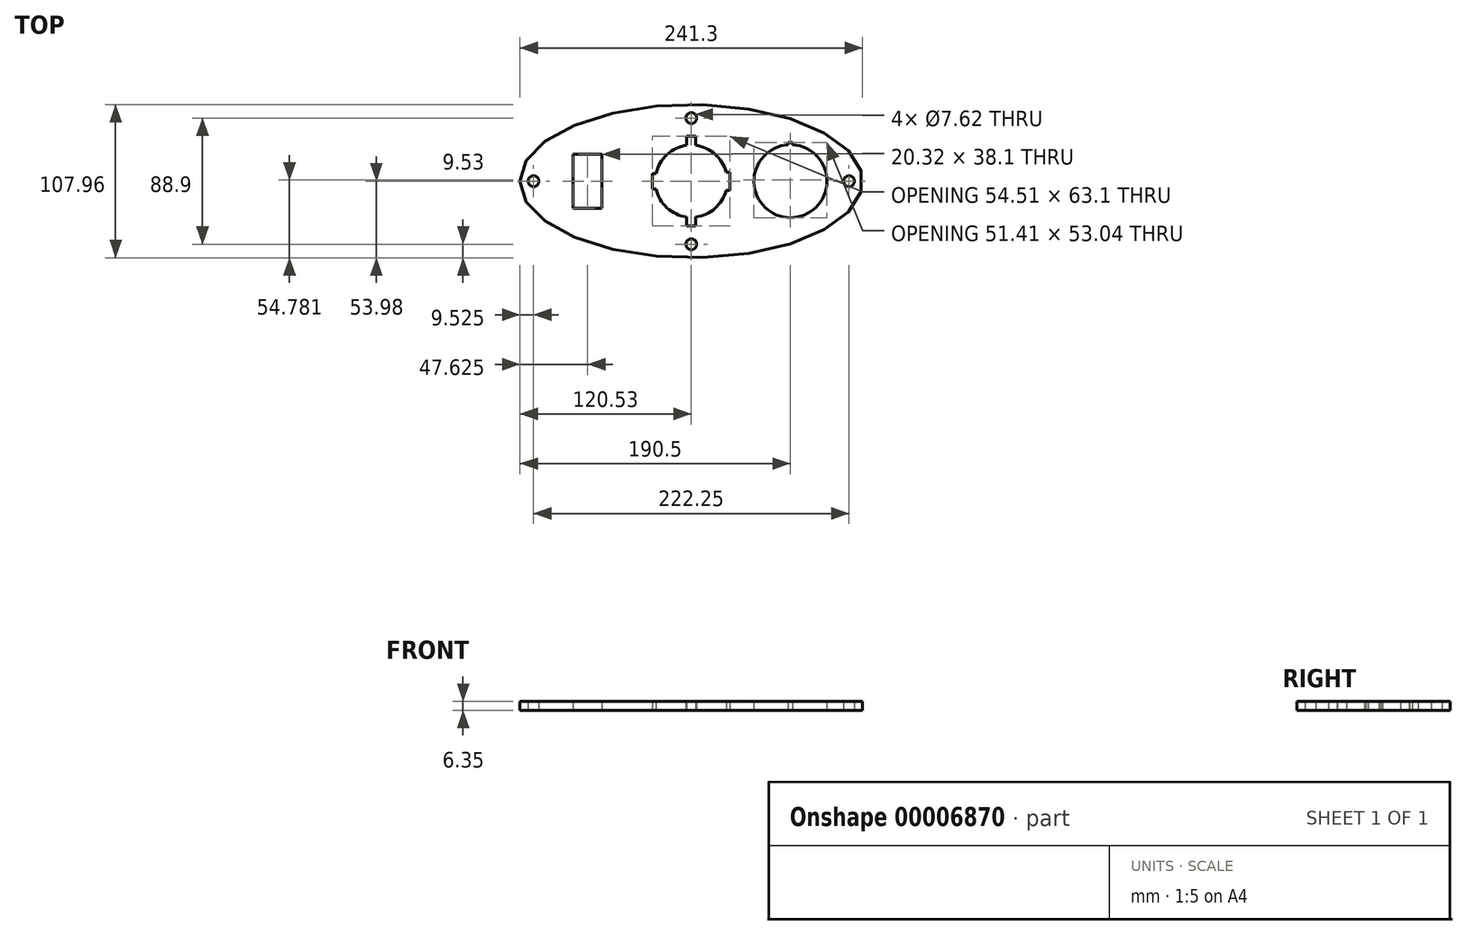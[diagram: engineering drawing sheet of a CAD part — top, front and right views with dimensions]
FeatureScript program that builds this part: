
annotation { "Feature Type Name" : "Feature", "Feature Type Description" : "" }
export const myFeature = defineFeature(function(context is Context, id is Id, definition is map)
    precondition{}
    {
        {
            var Q0;
            Q0=qCreatedBy(makeId("Top.planeOp"),FACE);
            var sketch = newSketch(context, id + "F0", { "sketchPlane" : qUnion([Q0])});
            skLineSegment(sketch, "E0", {"start": v(12.7, 0) * mm, "end": v(-120.65, 0) * mm, "construction": true});
            skLineSegment(sketch, "E1", {"start": v(0, 0) * mm, "end": v(0, 53.98) * mm, "construction": true});
            skEllipse(sketch, "E2", {"center": v(0, 0) * mm, "majorRadius": 120.65 * mm, "minorRadius": 53.98 * mm, "majorAxis": v(-1, 0)});
            skArc(sketch, "E3", {"start": v(-24.83, -5.33) * mm, "mid": v(-17.17, -18.72) * mm, "end": v(-3.17, -25.2) * mm});
            skLineSegment(sketch, "E4.rect.bottom", {"start": v(-62.86, -19.05) * mm, "end": v(-83.18, -19.05) * mm});
            skLineSegment(sketch, "E4.rect.top", {"start": v(-62.86, 19.05) * mm, "end": v(-83.18, 19.05) * mm});
            skLineSegment(sketch, "E4.rect.left", {"start": v(-62.86, -19.05) * mm, "end": v(-62.86, 19.05) * mm});
            skLineSegment(sketch, "E4.rect.right", {"start": v(-83.18, -19.05) * mm, "end": v(-83.18, 19.05) * mm});
            skPoint(sketch, "E4.rect.middle", {"position": v(-73.02, 0) * mm});
            skLineSegment(sketch, "E5", {"start": v(0, 0) * mm, "end": v(0, 34.07) * mm, "construction": true});
            skLineSegment(sketch, "E6", {"start": v(0, 0) * mm, "end": v(0, -29.55) * mm, "construction": true});
            skLineSegment(sketch, "E7.top", {"start": v(-3.17, 31.55) * mm, "end": v(3.17, 31.55) * mm});
            skLineSegment(sketch, "E7.left", {"start": v(-3.17, 25.2) * mm, "end": v(-3.18, 31.55) * mm});
            skLineSegment(sketch, "E7.right", {"start": v(3.18, 25.2) * mm, "end": v(3.17, 31.55) * mm});
            skLineSegment(sketch, "E8.top", {"start": v(-3.17, -31.55) * mm, "end": v(3.17, -31.55) * mm});
            skLineSegment(sketch, "E8.left", {"start": v(-3.17, -25.2) * mm, "end": v(-3.17, -31.55) * mm});
            skLineSegment(sketch, "E8.right", {"start": v(3.18, -25.2) * mm, "end": v(3.18, -31.55) * mm});
            skLineSegment(sketch, "E9.bottom", {"start": v(0, -29.55) * mm, "end": v(0, -29.55) * mm});
            skLineSegment(sketch, "E9.top", {"start": v(0, -35.98) * mm, "end": v(0, -35.98) * mm});
            skLineSegment(sketch, "E9.left", {"start": v(0, -29.55) * mm, "end": v(0, -35.98) * mm});
            skLineSegment(sketch, "E9.right", {"start": v(0, -29.55) * mm, "end": v(0, -35.98) * mm, "construction": true});
            skLineSegment(sketch, "E10", {"start": v(0, 0) * mm, "end": v(120.65, 0) * mm, "construction": true});
            skLineSegment(sketch, "E11.bottom", {"start": v(24.6, 6.35) * mm, "end": v(27.13, 6.35) * mm});
            skLineSegment(sketch, "E11.top", {"start": v(24.6, -6.35) * mm, "end": v(27.13, -6.35) * mm});
            skLineSegment(sketch, "E11.left", {"start": v(24.6, 6.35) * mm, "end": v(24.6, -6.35) * mm, "construction": true});
            skLineSegment(sketch, "E11.right", {"start": v(27.13, 6.35) * mm, "end": v(27.13, -6.35) * mm});
            skLineSegment(sketch, "E12", {"start": v(38.64, 0) * mm, "end": v(0, 0) * mm, "construction": true});
            skLineSegment(sketch, "E13.bottom", {"start": v(-24.83, 5.33) * mm, "end": v(-27.37, 5.33) * mm});
            skLineSegment(sketch, "E13.top", {"start": v(-24.83, -5.33) * mm, "end": v(-27.37, -5.33) * mm});
            skLineSegment(sketch, "E13.left", {"start": v(-24.83, 5.33) * mm, "end": v(-24.83, -5.33) * mm, "construction": true});
            skLineSegment(sketch, "E13.right", {"start": v(-27.37, 5.33) * mm, "end": v(-27.37, -5.33) * mm});
            skArc(sketch, "E14.trimOffspring", {"start": v(24.6, 6.35) * mm, "mid": v(16.78, 19.07) * mm, "end": v(3.18, 25.2) * mm});
            skArc(sketch, "E15.trimOffspring", {"start": v(3.17, -25.2) * mm, "mid": v(16.78, -19.07) * mm, "end": v(24.6, -6.35) * mm});
            skArc(sketch, "E16.trimOffspring", {"start": v(-3.17, 25.2) * mm, "mid": v(-17.17, 18.72) * mm, "end": v(-24.83, 5.33) * mm});
            skArc(sketch, "E17", {"start": v(68.26, 25.67) * mm, "mid": v(69.85, -25.72) * mm, "end": v(71.44, 25.67) * mm});
            skLineSegment(sketch, "E18", {"start": v(68.26, 25.67) * mm, "end": v(68.26, 27.32) * mm});
            skLineSegment(sketch, "E19", {"start": v(68.26, 27.32) * mm, "end": v(71.44, 27.32) * mm});
            skLineSegment(sketch, "E20", {"start": v(71.44, 27.32) * mm, "end": v(71.44, 25.67) * mm});
            skCircle(sketch, "E21", {"center": v(69.85, 0) * mm, "radius": 28.58 * mm, "construction": true});
            skCircle(sketch, "E22", {"center": v(0, 0) * mm, "radius": 33.34 * mm, "construction": true});
            skLineSegment(sketch, "E23.rect.bottom", {"start": v(-85.4, -22.23) * mm, "end": v(-60.64, -22.23) * mm, "construction": true});
            skLineSegment(sketch, "E23.rect.top", {"start": v(-85.4, 22.22) * mm, "end": v(-60.64, 22.22) * mm, "construction": true});
            skLineSegment(sketch, "E23.rect.left", {"start": v(-85.4, -22.23) * mm, "end": v(-85.4, 22.22) * mm, "construction": true});
            skLineSegment(sketch, "E23.rect.right", {"start": v(-60.64, -22.23) * mm, "end": v(-60.64, 22.22) * mm, "construction": true});
            skCircle(sketch, "E24", {"center": v(0, 44.45) * mm, "radius": 3.81 * mm});
            skCircle(sketch, "E25", {"center": v(0, -44.45) * mm, "radius": 3.81 * mm});
            skCircle(sketch, "E26", {"center": v(111.13, 0) * mm, "radius": 3.81 * mm});
            skCircle(sketch, "E27", {"center": v(-111.13, 0) * mm, "radius": 3.81 * mm});
            skSolve(sketch);
        }
        {
            var Q0;
            Q0=makeQuery(id+"F0.imprint","IMPRINT",FACE,{"disambiguationData":[TD([[makeQuery(id+"F0.imprint","IMPRINT",EDGE,{"derivedFrom":sQuery(id+"F0.wireOp",EDGE,"E2")}),1.0]])]});
            var Q1;
            Q1=makeQuery(id+"F2zThYBp0WIrXpu_0.imprint","IMPRINT",FACE,{"disambiguationData":[TD([[makeQuery(id+"F2zThYBp0WIrXpu_0.imprint","IMPRINT",EDGE,{"derivedFrom":sQuery(id+"F2zThYBp0WIrXpu_0.wireOp",EDGE,"877eec4c-a9e1-4678-a78c-56eb265a68d1.top")}),-1.0]])]});
            var Q2;
            {var subQ0=sQuery(id+"F2zThYBp0WIrXpu_0.wireOp",EDGE,"877eec4c-a9e1-4678-a78c-56eb265a68d1.bottom");var subQ1=sQuery(id+"F2zThYBp0WIrXpu_0.wireOp",EDGE,"c7f11e4e-3d1a-4ef3-a7b6-7e3971e68724");var subQ2=makeQuery(id+"F2zThYBp0WIrXpu_0.imprint","INTERSECT",VERTEX,{"derivedFrom":[subQ1,subQ0]});Q2=makeQuery(id+"F2zThYBp0WIrXpu_0.imprint","IMPRINT",FACE,{"disambiguationData":[TD([[makeQuery(id+"F2zThYBp0WIrXpu_0.imprint","IMPRINT",EDGE,{"disambiguationData":[TD([[subQ2,1.0]])],"derivedFrom":subQ1}),1.0]])]});}
            extrude(context, id + "F1", {"entities" : qUnion([Q0, Q1, Q2]), "depth" : 6.35 * mm});
        }
    });
